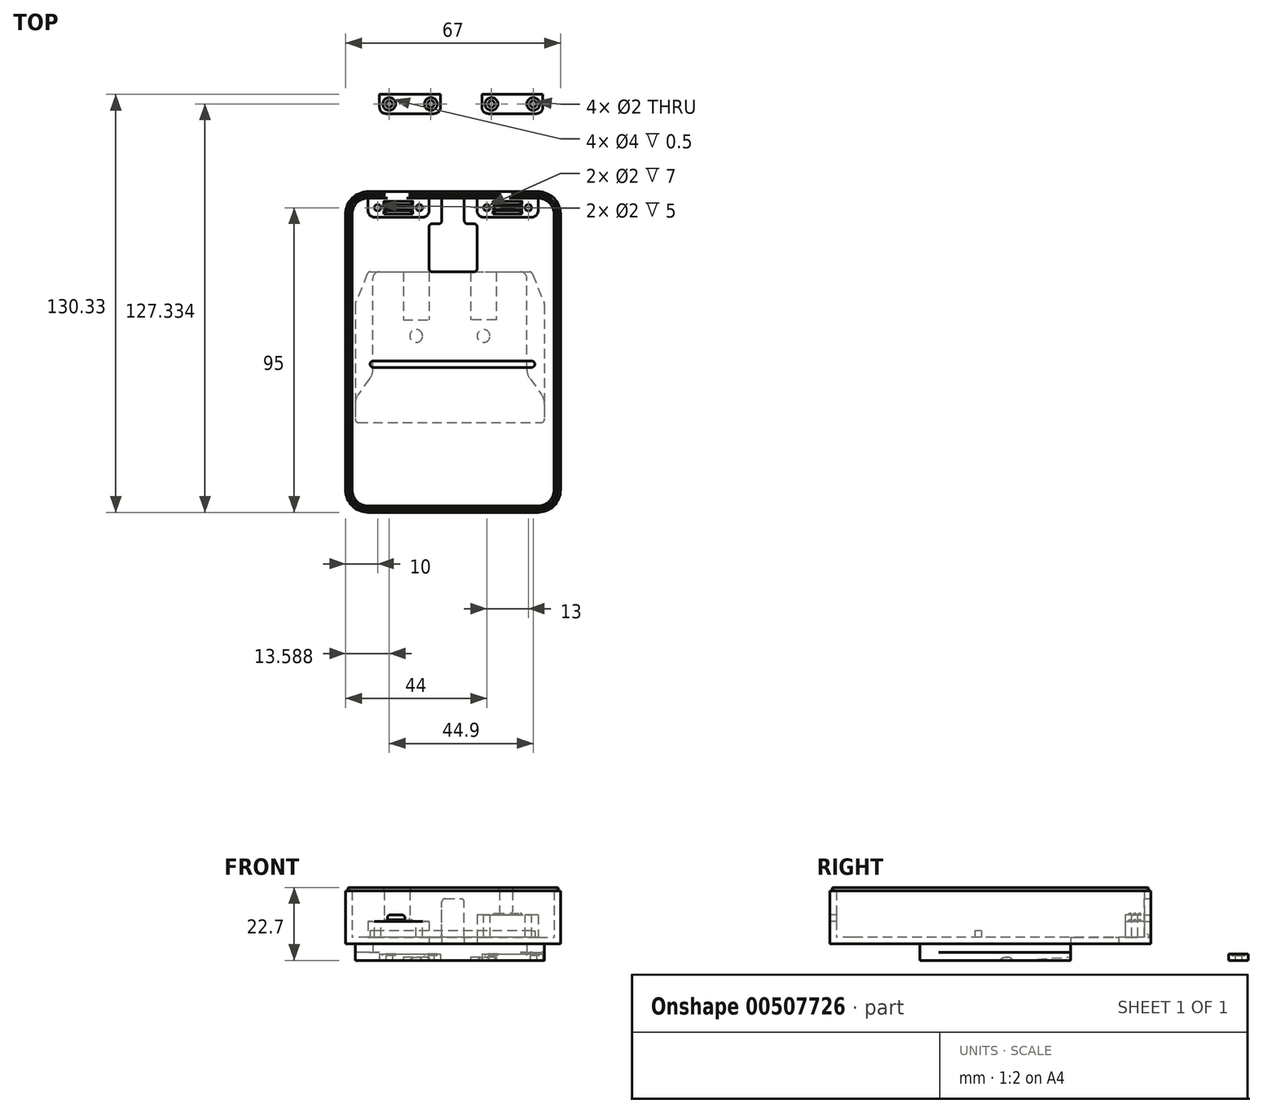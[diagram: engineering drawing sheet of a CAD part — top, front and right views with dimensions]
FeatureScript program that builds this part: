
annotation { "Feature Type Name" : "Feature", "Feature Type Description" : "" }
export const myFeature = defineFeature(function(context is Context, id is Id, definition is map)
    precondition{}
    {
        {
            var Q0;
            Q0=qCreatedBy(makeId("Top.planeOp"),FACE);
            var sketch = newSketch(context, id + "F0", { "sketchPlane" : qUnion([Q0])});
            skLineSegment(sketch, "E0.bottom", {"start": v(4, 0) * mm, "end": v(55, 0) * mm});
            skLineSegment(sketch, "E0.top", {"start": v(0, -47) * mm, "end": v(59, -47) * mm});
            skLineSegment(sketch, "E0.left", {"start": v(0, -10) * mm, "end": v(0, -47) * mm});
            skLineSegment(sketch, "E0.right", {"start": v(59, -10) * mm, "end": v(59, -47) * mm});
            skLineSegment(sketch, "E1", {"start": v(4, 0) * mm, "end": v(0, -10) * mm});
            skPoint(sketch, "E2.orphan", {"position": v(0, 0) * mm});
            skLineSegment(sketch, "E3", {"start": v(55, 0) * mm, "end": v(59, -10) * mm});
            skPoint(sketch, "E4.orphan", {"position": v(59, 0) * mm});
            skSolve(sketch);
        }
        {
            var Q0;
            Q0=makeQuery(id+"F0.imprint","IMPRINT",FACE,{"disambiguationData":[TD([[makeQuery(id+"F0.imprint","IMPRINT",EDGE,{"derivedFrom":sQuery(id+"F0.wireOp",EDGE,"E0.bottom")}),-1.0]])]});
            extrude(context, id + "F1", {"entities" : qUnion([Q0]), "depth" : 2.5 * mm, "offsetDistance" : 25 * mm});
        }
        {
            var Q0;
            Q0=makeQuery(id+"F1.opExtrude","CAP_FACE",FACE,{"disambiguationData":[OSD([sQuery(id+"F0.wireOp",EDGE,"E0.bottom"),sQuery(id+"F0.wireOp",EDGE,"E0.top"),sQuery(id+"F0.wireOp",EDGE,"E0.left"),sQuery(id+"F0.wireOp",EDGE,"E0.right"),sQuery(id+"F0.wireOp",EDGE,"E1"),sQuery(id+"F0.wireOp",EDGE,"E3")])],"isStart":false});
            var sketch = newSketch(context, id + "F2", { "sketchPlane" : qUnion([Q0])});
            skLineSegment(sketch, "E5.bottom", {"start": v(0, -47) * mm, "end": v(59, -47) * mm});
            skLineSegment(sketch, "E5.left", {"start": v(0, -47) * mm, "end": v(0, -39.5) * mm});
            skLineSegment(sketch, "E5.right", {"start": v(59, -47) * mm, "end": v(59, -39.5) * mm});
            skLineSegment(sketch, "E6.top", {"start": v(7.5, 0) * mm, "end": v(51.5, 0) * mm});
            skLineSegment(sketch, "E6.left", {"start": v(5.5, -32) * mm, "end": v(5.5, -2) * mm});
            skLineSegment(sketch, "E6.right", {"start": v(53.5, -32) * mm, "end": v(53.5, -2) * mm});
            skPoint(sketch, "E7.visualSharp", {"position": v(5.5, 0) * mm});
            skArc(sketch, "E7.filletArc", {"start": v(7.5, 0) * mm, "mid": v(6.09, -0.59) * mm, "end": v(5.5, -2) * mm});
            skPoint(sketch, "E8.visualSharp", {"position": v(53.5, 0) * mm});
            skArc(sketch, "E8.filletArc", {"start": v(53.5, -2) * mm, "mid": v(52.91, -0.59) * mm, "end": v(51.5, 0) * mm});
            skLineSegment(sketch, "E9", {"start": v(53.5, -32) * mm, "end": v(59, -39.5) * mm});
            skLineSegment(sketch, "E10", {"start": v(5.5, -32) * mm, "end": v(0, -39.5) * mm});
            skPoint(sketch, "E11.orphan", {"position": v(0, -32) * mm});
            skPoint(sketch, "E12.orphan", {"position": v(59, -32) * mm});
            skSolve(sketch);
        }
        {
            var Q0;
            Q0=makeQuery(id+"F2.imprint","IMPRINT",FACE,{"disambiguationData":[TD([[makeQuery(id+"F2.imprint","IMPRINT",EDGE,{"derivedFrom":sQuery(id+"F2.wireOp",EDGE,"E5.bottom")}),1.0]])]});
            extrude(context, id + "F3", {"entities" : qUnion([Q0]), "operationType" : NewBodyOperationType.ADD, "depth" : 2.7 * mm, "offsetDistance" : 25 * mm});
        }
        {
            var Q0;
            Q0=makeQuery(id+"F3.opExtrude","CAP_FACE",FACE,{"disambiguationData":[OSD([sQuery(id+"F2.wireOp",EDGE,"E5.bottom"),sQuery(id+"F2.wireOp",EDGE,"E5.left"),sQuery(id+"F2.wireOp",EDGE,"E5.right"),sQuery(id+"F2.wireOp",EDGE,"E6.top"),sQuery(id+"F2.wireOp",EDGE,"E6.left"),sQuery(id+"F2.wireOp",EDGE,"E6.right"),sQuery(id+"F2.wireOp",EDGE,"E7.filletArc"),sQuery(id+"F2.wireOp",EDGE,"E8.filletArc"),sQuery(id+"F2.wireOp",EDGE,"E9"),sQuery(id+"F2.wireOp",EDGE,"E10")])],"isStart":false});
            var sketch = newSketch(context, id + "F4", { "sketchPlane" : qUnion([Q0])});
            skLineSegment(sketch, "E13.bottom", {"start": v(57, -75) * mm, "end": v(4, -75) * mm});
            skLineSegment(sketch, "E13.top", {"start": v(57, 25) * mm, "end": v(35, 25) * mm});
            skLineSegment(sketch, "E13.left", {"start": v(64, -68) * mm, "end": v(64, 18) * mm});
            skLineSegment(sketch, "E13.right", {"start": v(-3, -68) * mm, "end": v(-3, 18) * mm});
            skPoint(sketch, "E14.visualSharp", {"position": v(-3, 25) * mm});
            skArc(sketch, "E14.filletArc", {"start": v(4, 25) * mm, "mid": v(-0.95, 22.95) * mm, "end": v(-3, 18) * mm});
            skPoint(sketch, "E15.visualSharp", {"position": v(64, 25) * mm});
            skArc(sketch, "E15.filletArc", {"start": v(64, 18) * mm, "mid": v(61.95, 22.95) * mm, "end": v(57, 25) * mm});
            skPoint(sketch, "E16.visualSharp", {"position": v(64, -75) * mm});
            skArc(sketch, "E16.filletArc", {"start": v(57, -75) * mm, "mid": v(61.95, -72.95) * mm, "end": v(64, -68) * mm});
            skPoint(sketch, "E17.visualSharp", {"position": v(-3, -75) * mm});
            skArc(sketch, "E17.filletArc", {"start": v(-3, -68) * mm, "mid": v(-0.95, -72.95) * mm, "end": v(4, -75) * mm});
            skLineSegment(sketch, "E18.top", {"start": v(27, 0) * mm, "end": v(34, 0) * mm});
            skLineSegment(sketch, "E18.left", {"start": v(27, 24) * mm, "end": v(27, 16) * mm});
            skLineSegment(sketch, "E18.right", {"start": v(34, 24) * mm, "end": v(34, 16) * mm});
            skLineSegment(sketch, "E19.filletArc", {"start": v(27, 0) * mm, "end": v(27, 0) * mm});
            skLineSegment(sketch, "E20.filletArc", {"start": v(34, 0) * mm, "end": v(34, 0) * mm});
            skLineSegment(sketch, "E21.trimOffspring", {"start": v(26, 25) * mm, "end": v(4, 25) * mm});
            skPoint(sketch, "E22.visualSharp", {"position": v(27, 25) * mm});
            skArc(sketch, "E22.filletArc", {"start": v(27, 24) * mm, "mid": v(26.7, 24.7) * mm, "end": v(26, 25) * mm});
            skPoint(sketch, "E23.visualSharp", {"position": v(34, 25) * mm});
            skArc(sketch, "E23.filletArc", {"start": v(35, 25) * mm, "mid": v(34.3, 24.7) * mm, "end": v(34, 24) * mm});
            skPoint(sketch, "E24", {"position": v(34, 15) * mm});
            skLineSegment(sketch, "E25", {"start": v(34, 0) * mm, "end": v(37, 0) * mm});
            skLineSegment(sketch, "E26", {"start": v(38, 1) * mm, "end": v(38, 14) * mm});
            skLineSegment(sketch, "E27", {"start": v(37, 15) * mm, "end": v(35, 15) * mm});
            skPoint(sketch, "E28", {"position": v(27, 15) * mm});
            skLineSegment(sketch, "E29", {"start": v(26, 15) * mm, "end": v(24, 15) * mm});
            skLineSegment(sketch, "E30", {"start": v(23, 14) * mm, "end": v(23, 1) * mm});
            skLineSegment(sketch, "E31", {"start": v(24, 0) * mm, "end": v(27, 0) * mm});
            skPoint(sketch, "E32.visualSharp", {"position": v(23, 15) * mm});
            skArc(sketch, "E32.filletArc", {"start": v(24, 15) * mm, "mid": v(23.3, 14.7) * mm, "end": v(23, 14) * mm});
            skPoint(sketch, "E33.visualSharp", {"position": v(23, 0) * mm});
            skArc(sketch, "E33.filletArc", {"start": v(23, 1) * mm, "mid": v(23.3, 0.3) * mm, "end": v(24, 0) * mm});
            skPoint(sketch, "E34.visualSharp", {"position": v(38, 0) * mm});
            skArc(sketch, "E34.filletArc", {"start": v(37, 0) * mm, "mid": v(37.7, 0.3) * mm, "end": v(38, 1) * mm});
            skPoint(sketch, "E35.visualSharp", {"position": v(38, 15) * mm});
            skArc(sketch, "E35.filletArc", {"start": v(38, 14) * mm, "mid": v(37.7, 14.7) * mm, "end": v(37, 15) * mm});
            skArc(sketch, "E36.filletArc", {"start": v(26, 15) * mm, "mid": v(26.7, 15.3) * mm, "end": v(27, 16) * mm});
            skArc(sketch, "E37.filletArc", {"start": v(34, 16) * mm, "mid": v(34.3, 15.3) * mm, "end": v(35, 15) * mm});
            skSolve(sketch);
        }
        {
            var Q0;
            Q0=qSketchRegion(id+"F4",true);
            extrude(context, id + "F5", {"entities" : qUnion([Q0]), "operationType" : NewBodyOperationType.ADD, "depth" : 2 * mm, "offsetDistance" : 25 * mm});
        }
        {
            var Q0;
            Q0=makeQuery(id+"F5.opExtrude","CAP_FACE",FACE,{"disambiguationData":[OSD([sQuery(id+"F4.wireOp",EDGE,"E13.bottom"),sQuery(id+"F4.wireOp",EDGE,"E13.top"),sQuery(id+"F4.wireOp",EDGE,"E13.left"),sQuery(id+"F4.wireOp",EDGE,"E13.right"),sQuery(id+"F4.wireOp",EDGE,"E14.filletArc"),sQuery(id+"F4.wireOp",EDGE,"E15.filletArc"),sQuery(id+"F4.wireOp",EDGE,"E16.filletArc"),sQuery(id+"F4.wireOp",EDGE,"E17.filletArc"),sQuery(id+"F4.wireOp",EDGE,"E18.top"),sQuery(id+"F4.wireOp",EDGE,"E18.left"),sQuery(id+"F4.wireOp",EDGE,"E18.right"),sQuery(id+"F4.wireOp",EDGE,"E19.filletArc"),sQuery(id+"F4.wireOp",EDGE,"E20.filletArc"),sQuery(id+"F4.wireOp",EDGE,"E21.trimOffspring"),sQuery(id+"F4.wireOp",EDGE,"E22.filletArc"),sQuery(id+"F4.wireOp",EDGE,"E23.filletArc")])],"isStart":false});
            var sketch = newSketch(context, id + "F6", { "sketchPlane" : qUnion([Q0])});
            skLineSegment(sketch, "E38.bottom", {"start": v(57, 25) * mm, "end": v(4, 25) * mm});
            skLineSegment(sketch, "E38.top", {"start": v(57, -75) * mm, "end": v(4, -75) * mm});
            skLineSegment(sketch, "E38.left", {"start": v(64, 18) * mm, "end": v(64, -68) * mm});
            skLineSegment(sketch, "E38.right", {"start": v(-3, 18) * mm, "end": v(-3, -68) * mm});
            skPoint(sketch, "E39.visualSharp", {"position": v(-3, 25) * mm});
            skArc(sketch, "E39.filletArc", {"start": v(4, 25) * mm, "mid": v(-0.95, 22.95) * mm, "end": v(-3, 18) * mm});
            skPoint(sketch, "E40.visualSharp", {"position": v(64, 25) * mm});
            skArc(sketch, "E40.filletArc", {"start": v(64, 18) * mm, "mid": v(61.95, 22.95) * mm, "end": v(57, 25) * mm});
            skPoint(sketch, "E41.visualSharp", {"position": v(64, -75) * mm});
            skArc(sketch, "E41.filletArc", {"start": v(57, -75) * mm, "mid": v(61.95, -72.95) * mm, "end": v(64, -68) * mm});
            skPoint(sketch, "E42.visualSharp", {"position": v(-3, -75) * mm});
            skArc(sketch, "E42.filletArc", {"start": v(-3, -68) * mm, "mid": v(-0.95, -72.95) * mm, "end": v(4, -75) * mm});
            skArc(sketch, "E43.0", {"start": v(62, 18) * mm, "mid": v(60.54, 21.54) * mm, "end": v(57, 23) * mm});
            skLineSegment(sketch, "E43.1", {"start": v(62, 18) * mm, "end": v(62, -68) * mm});
            skLineSegment(sketch, "E43.2", {"start": v(57, 23) * mm, "end": v(4, 23) * mm});
            skArc(sketch, "E43.3", {"start": v(57, -73) * mm, "mid": v(60.54, -71.54) * mm, "end": v(62, -68) * mm});
            skArc(sketch, "E43.4", {"start": v(4, 23) * mm, "mid": v(0.46, 21.54) * mm, "end": v(-1, 18) * mm});
            skLineSegment(sketch, "E43.5", {"start": v(-1, 18) * mm, "end": v(-1, -68) * mm});
            skArc(sketch, "E43.6", {"start": v(-1, -68) * mm, "mid": v(0.46, -71.54) * mm, "end": v(4, -73) * mm});
            skLineSegment(sketch, "E43.7", {"start": v(57, -73) * mm, "end": v(4, -73) * mm});
            skSolve(sketch);
        }
        {
            var Q0;
            Q0=qSketchRegion(id+"F6",true);
            extrude(context, id + "F7", {"entities" : qUnion([Q0]), "operationType" : NewBodyOperationType.ADD, "depth" : 14.5 * mm, "offsetDistance" : 25 * mm});
        }
        {
            var Q0;
            Q0=makeQuery(id+"F7.boolean.opBoolean","MERGE",FACE,{"derivedFrom":[makeQuery(id+"F5.opExtrude","SWEPT_FACE",FACE,{"disambiguationData":[OSD([sQuery(id+"F4.wireOp",EDGE,"E13.top")])]}),makeQuery(id+"F5.opExtrude","SWEPT_FACE",FACE,{"disambiguationData":[OSD([sQuery(id+"F4.wireOp",EDGE,"E21.trimOffspring")])]}),makeQuery(id+"F7.opExtrude","SWEPT_FACE",FACE,{"disambiguationData":[OSD([sQuery(id+"F6.wireOp",EDGE,"E38.bottom")])]})]});
            var sketch = newSketch(context, id + "F8", { "sketchPlane" : qUnion([Q0])});
            skLineSegment(sketch, "E44.bottom", {"start": v(-27, 7.2) * mm, "end": v(-34, 7.2) * mm});
            skLineSegment(sketch, "E44.top", {"start": v(-28, 19.2) * mm, "end": v(-33, 19.2) * mm});
            skLineSegment(sketch, "E44.left", {"start": v(-27, 7.2) * mm, "end": v(-27, 18.2) * mm});
            skLineSegment(sketch, "E44.right", {"start": v(-34, 7.2) * mm, "end": v(-34, 18.2) * mm});
            skPoint(sketch, "E45.visualSharp", {"position": v(-34, 19.2) * mm});
            skArc(sketch, "E45.filletArc", {"start": v(-33, 19.2) * mm, "mid": v(-33.7, 18.9) * mm, "end": v(-34, 18.2) * mm});
            skPoint(sketch, "E46.visualSharp", {"position": v(-27, 19.2) * mm});
            skArc(sketch, "E46.filletArc", {"start": v(-27, 18.2) * mm, "mid": v(-27.3, 18.9) * mm, "end": v(-28, 19.2) * mm});
            skLineSegment(sketch, "E47.bottom", {"start": v(-49, 21.7) * mm, "end": v(-45, 21.7) * mm});
            skLineSegment(sketch, "E47.top", {"start": v(-48, 14.2) * mm, "end": v(-46, 14.2) * mm});
            skLineSegment(sketch, "E47.left", {"start": v(-49, 21.7) * mm, "end": v(-49, 15.2) * mm});
            skLineSegment(sketch, "E47.right", {"start": v(-45, 21.7) * mm, "end": v(-45, 15.2) * mm});
            skPoint(sketch, "E48.visualSharp", {"position": v(-49, 14.2) * mm});
            skArc(sketch, "E48.filletArc", {"start": v(-49, 15.2) * mm, "mid": v(-48.7, 14.5) * mm, "end": v(-48, 14.2) * mm});
            skPoint(sketch, "E49.visualSharp", {"position": v(-45, 14.2) * mm});
            skArc(sketch, "E49.filletArc", {"start": v(-46, 14.2) * mm, "mid": v(-45.3, 14.5) * mm, "end": v(-45, 15.2) * mm});
            skLineSegment(sketch, "E50.bottom", {"start": v(-9, 21.7) * mm, "end": v(-17, 21.7) * mm});
            skLineSegment(sketch, "E50.top", {"start": v(-10, 12.2) * mm, "end": v(-16, 12.2) * mm});
            skLineSegment(sketch, "E50.left", {"start": v(-9, 21.7) * mm, "end": v(-9, 13.2) * mm});
            skLineSegment(sketch, "E50.right", {"start": v(-17, 21.7) * mm, "end": v(-17, 13.2) * mm});
            skPoint(sketch, "E51.visualSharp", {"position": v(-17, 12.2) * mm});
            skArc(sketch, "E51.filletArc", {"start": v(-17, 13.2) * mm, "mid": v(-16.7, 12.5) * mm, "end": v(-16, 12.2) * mm});
            skPoint(sketch, "E52.visualSharp", {"position": v(-9, 12.2) * mm});
            skArc(sketch, "E52.filletArc", {"start": v(-10, 12.2) * mm, "mid": v(-9.3, 12.5) * mm, "end": v(-9, 13.2) * mm});
            skSolve(sketch);
        }
        {
            var Q0;
            Q0=makeQuery(id+"FvWDrRj3cYPkLqx_1.boolean.opBoolean","MERGE",FACE,{"derivedFrom":[makeQuery(id+"F5.opExtrude","CAP_FACE",FACE,{"disambiguationData":[OSD([sQuery(id+"F4.wireOp",EDGE,"E13.bottom"),sQuery(id+"F4.wireOp",EDGE,"E13.top"),sQuery(id+"F4.wireOp",EDGE,"E13.left"),sQuery(id+"F4.wireOp",EDGE,"E13.right"),sQuery(id+"F4.wireOp",EDGE,"E14.filletArc"),sQuery(id+"F4.wireOp",EDGE,"E15.filletArc"),sQuery(id+"F4.wireOp",EDGE,"E16.filletArc"),sQuery(id+"F4.wireOp",EDGE,"E17.filletArc"),sQuery(id+"F4.wireOp",EDGE,"E18.top"),sQuery(id+"F4.wireOp",EDGE,"E18.left"),sQuery(id+"F4.wireOp",EDGE,"E18.right"),sQuery(id+"F4.wireOp",EDGE,"E19.filletArc"),sQuery(id+"F4.wireOp",EDGE,"E20.filletArc"),sQuery(id+"F4.wireOp",EDGE,"E21.trimOffspring"),sQuery(id+"F4.wireOp",EDGE,"E22.filletArc"),sQuery(id+"F4.wireOp",EDGE,"E23.filletArc")])],"isStart":false}),makeQuery(id+"FvWDrRj3cYPkLqx_1.opExtrude","SWEPT_FACE",FACE,{"disambiguationData":[OSD([sQuery(id+"F8.wireOp",EDGE,"E44.bottom")])]})]});
            var sketch = newSketch(context, id + "F9", { "sketchPlane" : qUnion([Q0])});
            skLineSegment(sketch, "E53.bottom", {"start": v(54.99, -29.8) * mm, "end": v(5.63, -29.8) * mm});
            skLineSegment(sketch, "E53.top", {"start": v(54.99, -27.8) * mm, "end": v(5.63, -27.8) * mm});
            skLineSegment(sketch, "E53.left", {"start": v(55.99, -28.8) * mm, "end": v(55.99, -28.8) * mm});
            skLineSegment(sketch, "E53.right", {"start": v(4.63, -28.8) * mm, "end": v(4.63, -28.8) * mm});
            skPoint(sketch, "E54.visualSharp", {"position": v(4.63, -27.8) * mm});
            skArc(sketch, "E54.filletArc", {"start": v(5.63, -27.8) * mm, "mid": v(4.92, -28.1) * mm, "end": v(4.63, -28.8) * mm});
            skPoint(sketch, "E55.visualSharp", {"position": v(4.63, -29.8) * mm});
            skArc(sketch, "E55.filletArc", {"start": v(4.63, -28.8) * mm, "mid": v(4.92, -29.5) * mm, "end": v(5.63, -29.8) * mm});
            skPoint(sketch, "E56.visualSharp", {"position": v(55.99, -27.8) * mm});
            skArc(sketch, "E56.filletArc", {"start": v(55.99, -28.8) * mm, "mid": v(55.7, -28.1) * mm, "end": v(54.99, -27.8) * mm});
            skPoint(sketch, "E57.visualSharp", {"position": v(55.99, -29.8) * mm});
            skArc(sketch, "E57.filletArc", {"start": v(54.99, -29.8) * mm, "mid": v(55.7, -29.5) * mm, "end": v(55.99, -28.8) * mm});
            skSolve(sketch);
        }
        {
            var Q0;
            Q0=qSketchRegion(id+"F9",true);
            var Q1;
            Q1=qSketchRegion(id+"F11",true);
            extrude(context, id + "F10", {"entities" : qUnion([Q0, Q1]), "operationType" : NewBodyOperationType.ADD, "depth" : 2 * mm});
        }
        {
            var Q0;
            Q0=makeQuery(id+"FvWDrRj3cYPkLqx_1.boolean.opBoolean","MERGE",FACE,{"derivedFrom":[makeQuery(id+"F5.opExtrude","CAP_FACE",FACE,{"disambiguationData":[OSD([sQuery(id+"F4.wireOp",EDGE,"E13.bottom"),sQuery(id+"F4.wireOp",EDGE,"E13.top"),sQuery(id+"F4.wireOp",EDGE,"E13.left"),sQuery(id+"F4.wireOp",EDGE,"E13.right"),sQuery(id+"F4.wireOp",EDGE,"E14.filletArc"),sQuery(id+"F4.wireOp",EDGE,"E15.filletArc"),sQuery(id+"F4.wireOp",EDGE,"E16.filletArc"),sQuery(id+"F4.wireOp",EDGE,"E17.filletArc"),sQuery(id+"F4.wireOp",EDGE,"E18.top"),sQuery(id+"F4.wireOp",EDGE,"E18.left"),sQuery(id+"F4.wireOp",EDGE,"E18.right"),sQuery(id+"F4.wireOp",EDGE,"E19.filletArc"),sQuery(id+"F4.wireOp",EDGE,"E20.filletArc"),sQuery(id+"F4.wireOp",EDGE,"E21.trimOffspring"),sQuery(id+"F4.wireOp",EDGE,"E22.filletArc"),sQuery(id+"F4.wireOp",EDGE,"E23.filletArc")])],"isStart":false}),makeQuery(id+"FvWDrRj3cYPkLqx_1.opExtrude","SWEPT_FACE",FACE,{"disambiguationData":[OSD([sQuery(id+"F8.wireOp",EDGE,"E44.bottom")])]})]});
            var sketch = newSketch(context, id + "F11", { "sketchPlane" : qUnion([Q0])});
            skSolve(sketch);
        }
        {
            var Q0;
            Q0=makeQuery(id+"F8.imprint","IMPRINT",FACE,{"disambiguationData":[TD([[makeQuery(id+"F8.imprint","IMPRINT",EDGE,{"derivedFrom":sQuery(id+"F8.wireOp",EDGE,"E47.bottom")}),-1.0]])]});
            var Q1;
            Q1=makeQuery(id+"F8.imprint","IMPRINT",FACE,{"disambiguationData":[TD([[makeQuery(id+"F8.imprint","IMPRINT",EDGE,{"derivedFrom":sQuery(id+"F8.wireOp",EDGE,"E44.top")}),1.0]])]});
            var Q2;
            Q2=makeQuery(id+"F8.imprint","IMPRINT",FACE,{"disambiguationData":[TD([[makeQuery(id+"F8.imprint","IMPRINT",EDGE,{"derivedFrom":sQuery(id+"F8.wireOp",EDGE,"E50.bottom")}),-1.0]])]});
            extrude(context, id + "F12", {"entities" : qUnion([Q0, Q1, Q2]), "operationType" : NewBodyOperationType.REMOVE, "oppositeDirection" : true, "depth" : 2 * mm});
        }
        {
            var Q0;
            Q0=makeQuery(id+"F7.boolean.opBoolean","MERGE",FACE,{"derivedFrom":[makeQuery(id+"F5.opExtrude","SWEPT_FACE",FACE,{"disambiguationData":[OSD([sQuery(id+"F4.wireOp",EDGE,"E13.bottom")])]}),makeQuery(id+"F7.opExtrude","SWEPT_FACE",FACE,{"disambiguationData":[OSD([sQuery(id+"F6.wireOp",EDGE,"E38.top")])]})]});
            var sketch = newSketch(context, id + "F13", { "sketchPlane" : qUnion([Q0])});
            skLineSegment(sketch, "E58.bottom", {"start": v(11, 14.2) * mm, "end": v(14.5, 14.2) * mm});
            skLineSegment(sketch, "E58.top", {"start": v(11, 12.2) * mm, "end": v(14.5, 12.2) * mm});
            skLineSegment(sketch, "E58.left", {"start": v(10, 13.2) * mm, "end": v(10, 13.2) * mm});
            skLineSegment(sketch, "E58.right", {"start": v(15.5, 13.2) * mm, "end": v(15.5, 13.2) * mm});
            skPoint(sketch, "E59.visualSharp", {"position": v(10, 14.2) * mm});
            skArc(sketch, "E59.filletArc", {"start": v(11, 14.2) * mm, "mid": v(10.3, 13.9) * mm, "end": v(10, 13.2) * mm});
            skPoint(sketch, "E60.visualSharp", {"position": v(10, 12.2) * mm});
            skArc(sketch, "E60.filletArc", {"start": v(10, 13.2) * mm, "mid": v(10.3, 12.5) * mm, "end": v(11, 12.2) * mm});
            skPoint(sketch, "E61.visualSharp", {"position": v(15.5, 14.2) * mm});
            skArc(sketch, "E61.filletArc", {"start": v(15.5, 13.2) * mm, "mid": v(15.2, 13.9) * mm, "end": v(14.5, 14.2) * mm});
            skPoint(sketch, "E62.visualSharp", {"position": v(15.5, 12.2) * mm});
            skArc(sketch, "E62.filletArc", {"start": v(14.5, 12.2) * mm, "mid": v(15.2, 12.5) * mm, "end": v(15.5, 13.2) * mm});
            skSolve(sketch);
        }
        {
            var Q0;
            Q0=makeQuery(id+"F13.imprint","IMPRINT",FACE,{"disambiguationData":[TD([[makeQuery(id+"F13.imprint","IMPRINT",EDGE,{"derivedFrom":sQuery(id+"F13.wireOp",EDGE,"E58.bottom")}),-1.0]])]});
            extrude(context, id + "F14", {"entities" : qUnion([Q0]), "operationType" : NewBodyOperationType.REMOVE, "oppositeDirection" : true, "depth" : 2 * mm, "offsetDistance" : 25 * mm});
        }
        {
            var Q0;
            Q0=makeQuery(id+"F3.boolean.opBoolean","MERGE",EDGE,{"derivedFrom":[makeQuery(id+"F1.opExtrude","SWEPT_EDGE",EDGE,{"disambiguationData":[OSD([sQuery(id+"F0.wireOp",EDGE,"E0.top"),sQuery(id+"F0.wireOp",EDGE,"E0.left")])]}),makeQuery(id+"F3.opExtrude","SWEPT_EDGE",EDGE,{"disambiguationData":[OSD([sQuery(id+"F2.wireOp",EDGE,"E5.bottom"),sQuery(id+"F2.wireOp",EDGE,"E5.left")])]})]});
            var Q1;
            Q1=makeQuery(id+"F3.boolean.opBoolean","MERGE",EDGE,{"derivedFrom":[makeQuery(id+"F1.opExtrude","SWEPT_EDGE",EDGE,{"disambiguationData":[OSD([sQuery(id+"F0.wireOp",EDGE,"E0.top"),sQuery(id+"F0.wireOp",EDGE,"E0.right")])]}),makeQuery(id+"F3.opExtrude","SWEPT_EDGE",EDGE,{"disambiguationData":[OSD([sQuery(id+"F2.wireOp",EDGE,"E5.bottom"),sQuery(id+"F2.wireOp",EDGE,"E5.right")])]})]});
            var Q2;
            Q2=makeQuery(id+"F1.opExtrude","SWEPT_EDGE",EDGE,{"disambiguationData":[OSD([sQuery(id+"F0.wireOp",EDGE,"E0.bottom"),sQuery(id+"F0.wireOp",EDGE,"E1")])]});
            var Q3;
            Q3=makeQuery(id+"F1.opExtrude","SWEPT_EDGE",EDGE,{"disambiguationData":[OSD([sQuery(id+"F0.wireOp",EDGE,"E0.bottom"),sQuery(id+"F0.wireOp",EDGE,"E3")])]});
            var Q4;
            Q4=makeQuery(id+"F1.opExtrude","SWEPT_EDGE",EDGE,{"disambiguationData":[OSD([sQuery(id+"F0.wireOp",EDGE,"E0.right"),sQuery(id+"F0.wireOp",EDGE,"E3")])]});
            var Q5;
            Q5=makeQuery(id+"F1.opExtrude","SWEPT_EDGE",EDGE,{"disambiguationData":[OSD([sQuery(id+"F0.wireOp",EDGE,"E0.left"),sQuery(id+"F0.wireOp",EDGE,"E1")])]});
            fillet(context, id + "F15", {"entities" : qUnion([Q0, Q1, Q2, Q3, Q4, Q5]), "radius" : 1 * mm, "tangentPropagation" : true, "allowEdgeOverflow" : false});
        }
        {
            var Q0;
            Q0=makeQuery(id+"F3.opExtrude","SWEPT_EDGE",EDGE,{"disambiguationData":[OSD([sQuery(id+"F0.wireOp",EDGE,"E0.left"),sQuery(id+"F2.wireOp",EDGE,"E5.left"),sQuery(id+"F2.wireOp",EDGE,"E10")])]});
            var Q1;
            Q1=makeQuery(id+"F3.opExtrude","SWEPT_EDGE",EDGE,{"disambiguationData":[OSD([sQuery(id+"F0.wireOp",EDGE,"E0.right"),sQuery(id+"F2.wireOp",EDGE,"E5.right"),sQuery(id+"F2.wireOp",EDGE,"E9")])]});
            var Q2;
            Q2=makeQuery(id+"F3.opExtrude","SWEPT_EDGE",EDGE,{"disambiguationData":[OSD([sQuery(id+"F2.wireOp",EDGE,"E6.right"),sQuery(id+"F2.wireOp",EDGE,"E9")])]});
            var Q3;
            Q3=makeQuery(id+"F3.opExtrude","SWEPT_EDGE",EDGE,{"disambiguationData":[OSD([sQuery(id+"F2.wireOp",EDGE,"E6.left"),sQuery(id+"F2.wireOp",EDGE,"E10")])]});
            fillet(context, id + "F16", {"entities" : qUnion([Q0, Q1, Q2, Q3]), "radius" : 5 * mm, "tangentPropagation" : true, "allowEdgeOverflow" : false});
        }
        {
            var Q0;
            Q0=makeQuery(id+"F1.opExtrude","CAP_FACE",FACE,{"disambiguationData":[OSD([sQuery(id+"F0.wireOp",EDGE,"E0.bottom"),sQuery(id+"F0.wireOp",EDGE,"E0.top"),sQuery(id+"F0.wireOp",EDGE,"E0.left"),sQuery(id+"F0.wireOp",EDGE,"E0.right"),sQuery(id+"F0.wireOp",EDGE,"E1"),sQuery(id+"F0.wireOp",EDGE,"E3")])],"isStart":true});
            var sketch = newSketch(context, id + "F17", { "sketchPlane" : qUnion([Q0])});
            skLineSegment(sketch, "E63.bottom", {"start": v(15, 0) * mm, "end": v(23, 0) * mm});
            skLineSegment(sketch, "E63.top", {"start": v(15, 15) * mm, "end": v(23, 15) * mm});
            skLineSegment(sketch, "E63.left", {"start": v(15, 0) * mm, "end": v(15, 15) * mm});
            skLineSegment(sketch, "E63.right", {"start": v(23, 0) * mm, "end": v(23, 15) * mm});
            skLineSegment(sketch, "E64.bottom", {"start": v(44, 0) * mm, "end": v(36, 0) * mm});
            skLineSegment(sketch, "E64.top", {"start": v(44, 15) * mm, "end": v(36, 15) * mm});
            skLineSegment(sketch, "E64.left", {"start": v(44, 0) * mm, "end": v(44, 15) * mm});
            skLineSegment(sketch, "E64.right", {"start": v(36, 0) * mm, "end": v(36, 15) * mm});
            skSolve(sketch);
        }
        {
            var Q0;
            Q0=makeQuery(id+"F1.opExtrude","CAP_FACE",FACE,{"disambiguationData":[OSD([sQuery(id+"F0.wireOp",EDGE,"E0.bottom"),sQuery(id+"F0.wireOp",EDGE,"E0.top"),sQuery(id+"F0.wireOp",EDGE,"E0.left"),sQuery(id+"F0.wireOp",EDGE,"E0.right"),sQuery(id+"F0.wireOp",EDGE,"E1"),sQuery(id+"F0.wireOp",EDGE,"E3")])],"isStart":true});
            var sketch = newSketch(context, id + "F18", { "sketchPlane" : qUnion([Q0])});
            skCircle(sketch, "E65", {"center": v(19, 20) * mm, "radius": 2 * mm});
            skCircle(sketch, "E66", {"center": v(40, 20) * mm, "radius": 2 * mm});
            skSolve(sketch);
        }
        {
            var Q0;
            Q0=qSketchRegion(id+"F18",true);
            extrude(context, id + "F19", {"entities" : qUnion([Q0]), "operationType" : NewBodyOperationType.REMOVE, "oppositeDirection" : true, "depth" : 1 * mm});
        }
        {
            var Q0;
            Q0=makeQuery(id+"F17.imprint","IMPRINT",FACE,{"disambiguationData":[TD([[makeQuery(id+"F17.imprint","IMPRINT",EDGE,{"derivedFrom":sQuery(id+"F17.wireOp",EDGE,"E64.bottom")}),1.0]])]});
            var Q1;
            Q1=makeQuery(id+"F17.imprint","IMPRINT",FACE,{"disambiguationData":[TD([[makeQuery(id+"F17.imprint","IMPRINT",EDGE,{"derivedFrom":sQuery(id+"F17.wireOp",EDGE,"E63.bottom")}),1.0]])]});
            extrude(context, id + "F20", {"entities" : qUnion([Q0, Q1]), "operationType" : NewBodyOperationType.REMOVE, "oppositeDirection" : true, "depth" : 1.1 * mm});
        }
        {
            var Q0;
            Q0=makeQuery(id+"F20.boolean.opBoolean","COPY",EDGE,{"derivedFrom":makeQuery(id+"F20.opExtrude","CAP_EDGE",EDGE,{"disambiguationData":[OSD([sQuery(id+"F17.wireOp",EDGE,"E63.top")])],"isStart":false})});
            chamfer(context, id + "F21", {"entities" : qUnion([Q0]), "chamferType" : ChamferType.TWO_OFFSETS, "width1" : 1.1 * mm, "oppositeDirection" : false, "width2" : 15 * mm, "tangentPropagation" : true});
        }
        {
            var Q0;
            Q0=makeQuery(id+"F20.boolean.opBoolean","COPY",EDGE,{"derivedFrom":makeQuery(id+"F20.opExtrude","CAP_EDGE",EDGE,{"disambiguationData":[OSD([sQuery(id+"F17.wireOp",EDGE,"E64.top")])],"isStart":false})});
            chamfer(context, id + "F22", {"entities" : qUnion([Q0]), "chamferType" : ChamferType.TWO_OFFSETS, "width1" : 15 * mm, "oppositeDirection" : false, "width2" : 1.1 * mm, "tangentPropagation" : true});
        }
        {
            var Q0;
            Q0=makeQuery(id+"F19.boolean.opBoolean","COPY",EDGE,{"derivedFrom":makeQuery(id+"F19.opExtrude","CAP_EDGE",EDGE,{"disambiguationData":[OSD([sQuery(id+"F18.wireOp",EDGE,"E66")])],"isStart":false})});
            var Q1;
            Q1=makeQuery(id+"F19.boolean.opBoolean","COPY",EDGE,{"derivedFrom":makeQuery(id+"F19.opExtrude","CAP_EDGE",EDGE,{"disambiguationData":[OSD([sQuery(id+"F18.wireOp",EDGE,"E65")])],"isStart":false})});
            fillet(context, id + "F23", {"entities" : qUnion([Q0, Q1]), "radius" : 2 * mm, "tangentPropagation" : true, "allowEdgeOverflow" : false});
        }
        {
            var Q0;
            {var subQ0=sQuery(id+"F6.wireOp",EDGE,"E43.2");var subQ1=sQuery(id+"F6.wireOp",EDGE,"E43.1");var subQ2=sQuery(id+"F6.wireOp",EDGE,"E42.filletArc");var subQ3=sQuery(id+"F6.wireOp",EDGE,"E41.filletArc");var subQ4=sQuery(id+"F6.wireOp",EDGE,"E40.filletArc");var subQ5=sQuery(id+"F6.wireOp",EDGE,"E39.filletArc");var subQ6=sQuery(id+"F6.wireOp",EDGE,"E38.right");var subQ7=sQuery(id+"F6.wireOp",EDGE,"E38.left");var subQ8=sQuery(id+"F6.wireOp",EDGE,"E38.top");var subQ9=sQuery(id+"F6.wireOp",EDGE,"E43.4");var subQ10=sQuery(id+"F6.wireOp",EDGE,"E43.3");var subQ11=sQuery(id+"F6.wireOp",EDGE,"E38.bottom");var subQ12=sQuery(id+"F6.wireOp",EDGE,"E43.0");var subQ13=sQuery(id+"F6.wireOp",EDGE,"E43.5");var subQ14=sQuery(id+"F6.wireOp",EDGE,"E43.6");var subQ15=sQuery(id+"F6.wireOp",EDGE,"E43.7");Q0=makeQuery(id+"F12.boolean.opBoolean","SPLIT",FACE,{"disambiguationData":[TD([makeQuery(id+"F5.opExtrude","SWEPT_FACE",FACE,{"disambiguationData":[OSD([sQuery(id+"F4.wireOp",EDGE,"E13.bottom")])]})])],"derivedFrom":makeQuery(id+"F7.opExtrude","CAP_FACE",FACE,{"disambiguationData":[OSD([subQ11,subQ8,subQ7,subQ6,subQ5,subQ4,subQ3,subQ2,subQ12,subQ1,subQ0,subQ10,subQ9,subQ13,subQ14,subQ15])],"isStart":false})});}
            var sketch = newSketch(context, id + "F24", { "sketchPlane" : qUnion([Q0])});
            skLineSegment(sketch, "E67.0", {"start": v(57, 24.25) * mm, "end": v(49, 24.25) * mm});
            skArc(sketch, "E67.1", {"start": v(63.25, 18) * mm, "mid": v(61.42, 22.42) * mm, "end": v(57, 24.25) * mm});
            skLineSegment(sketch, "E67.2", {"start": v(63.25, -68) * mm, "end": v(63.25, 18) * mm});
            skArc(sketch, "E67.3", {"start": v(57, -74.25) * mm, "mid": v(61.42, -72.42) * mm, "end": v(63.25, -68) * mm});
            skLineSegment(sketch, "E67.4", {"start": v(57, -74.25) * mm, "end": v(4, -74.25) * mm});
            skLineSegment(sketch, "E67.5", {"start": v(9, 24.25) * mm, "end": v(4, 24.25) * mm});
            skArc(sketch, "E67.6", {"start": v(4, 24.25) * mm, "mid": v(-0.42, 22.42) * mm, "end": v(-2.25, 18) * mm});
            skLineSegment(sketch, "E67.7", {"start": v(-2.25, -68) * mm, "end": v(-2.25, 18) * mm});
            skArc(sketch, "E67.8", {"start": v(-2.25, -68) * mm, "mid": v(-0.42, -72.42) * mm, "end": v(4, -74.25) * mm});
            skLineSegment(sketch, "E68.0", {"start": v(57, 23.75) * mm, "end": v(49, 23.75) * mm});
            skArc(sketch, "E68.1", {"start": v(62.75, 18) * mm, "mid": v(61.07, 22.07) * mm, "end": v(57, 23.75) * mm});
            skLineSegment(sketch, "E68.2", {"start": v(62.75, 18) * mm, "end": v(62.75, -68) * mm});
            skArc(sketch, "E68.3", {"start": v(57, -73.75) * mm, "mid": v(61.07, -72.07) * mm, "end": v(62.75, -68) * mm});
            skLineSegment(sketch, "E68.4", {"start": v(57, -73.75) * mm, "end": v(4, -73.75) * mm});
            skLineSegment(sketch, "E68.5", {"start": v(9, 23.75) * mm, "end": v(4, 23.75) * mm});
            skArc(sketch, "E68.6", {"start": v(4, 23.75) * mm, "mid": v(-0.07, 22.07) * mm, "end": v(-1.75, 18) * mm});
            skLineSegment(sketch, "E68.7", {"start": v(-1.75, 18) * mm, "end": v(-1.75, -68) * mm});
            skArc(sketch, "E68.8", {"start": v(-1.75, -68) * mm, "mid": v(-0.07, -72.07) * mm, "end": v(4, -73.75) * mm});
            skLineSegment(sketch, "E69.0", {"start": v(45, 24.25) * mm, "end": v(17, 24.25) * mm});
            skLineSegment(sketch, "E70.0", {"start": v(45, 23.75) * mm, "end": v(17, 23.75) * mm});
            skLineSegment(sketch, "E71", {"start": v(17, 24.25) * mm, "end": v(17, 23.75) * mm});
            skLineSegment(sketch, "E72", {"start": v(45, 24.25) * mm, "end": v(45, 23.75) * mm});
            skSolve(sketch);
        }
        {
            var Q0;
            {var subQ2=sQuery(id+"F24.wireOp",EDGE,"E67.0");Q0=makeQuery(id+"F24.imprint","IMPRINT",FACE,{"disambiguationData":[TD([[makeQuery(id+"F24.imprint","IMPRINT",EDGE,{"derivedFrom":subQ2}),1.0]])]});}
            extrude(context, id + "F25", {"entities" : qUnion([Q0]), "operationType" : NewBodyOperationType.ADD, "depth" : 1 * mm, "offsetDistance" : 25 * mm});
        }
        {
            var Q0;
            Q0=qSketchRegion(id+"F24",true);
            extrude(context, id + "F26", {"entities" : qUnion([Q0]), "operationType" : NewBodyOperationType.ADD, "depth" : 1 * mm, "offsetDistance" : 25 * mm});
        }
        {
            var Q0;
            Q0=makeQuery(id+"F25.opExtrude","CAP_EDGE",EDGE,{"disambiguationData":[OSD([sQuery(id+"F6.wireOp",EDGE,"E38.bottom"),sQuery(id+"F8.wireOp",EDGE,"E47.bottom"),sQuery(id+"F8.wireOp",EDGE,"E47.left")])],"isStart":false});
            var Q1;
            Q1=makeQuery(id+"F26.opExtrude","CAP_EDGE",EDGE,{"disambiguationData":[OSD([sQuery(id+"F24.wireOp",EDGE,"E72")])],"isStart":false});
            var Q2;
            Q2=makeQuery(id+"F26.opExtrude","CAP_EDGE",EDGE,{"disambiguationData":[OSD([sQuery(id+"F24.wireOp",EDGE,"E71")])],"isStart":false});
            var Q3;
            Q3=makeQuery(id+"F25.opExtrude","CAP_EDGE",EDGE,{"disambiguationData":[OSD([sQuery(id+"F6.wireOp",EDGE,"E38.bottom"),sQuery(id+"F8.wireOp",EDGE,"E50.bottom"),sQuery(id+"F8.wireOp",EDGE,"E50.left")])],"isStart":false});
            var Q4;
            Q4=makeQuery(id+"F12.boolean.opBoolean","COPY",EDGE,{"derivedFrom":makeQuery(id+"F12.opExtrude","SWEPT_EDGE",EDGE,{"disambiguationData":[OSD([sQuery(id+"F8.wireOp",EDGE,"E44.bottom"),sQuery(id+"F8.wireOp",EDGE,"E44.right")])]})});
            var Q5;
            Q5=makeQuery(id+"F12.boolean.opBoolean","COPY",EDGE,{"derivedFrom":makeQuery(id+"F12.opExtrude","SWEPT_EDGE",EDGE,{"disambiguationData":[OSD([sQuery(id+"F8.wireOp",EDGE,"E44.bottom"),sQuery(id+"F8.wireOp",EDGE,"E44.left")])]})});
            fillet(context, id + "F27", {"entities" : qUnion([Q0, Q1, Q2, Q3, Q4, Q5]), "radius" : 1 * mm, "tangentPropagation" : true, "allowEdgeOverflow" : false});
        }
        {
            var Q0;
            {var subQ6=sQuery(id+"F4.wireOp",EDGE,"E18.top");Q0=makeQuery(id+"F11.imprint","IMPRINT",FACE,{"disambiguationData":[TD([[makeQuery(id+"F11.imprint","IMPRINT",EDGE,{"derivedFrom":makeQuery(id+"F5.opExtrude","CAP_EDGE",EDGE,{"disambiguationData":[OSD([subQ6])],"isStart":false})}),-1.0]])]});}
            var sketch = newSketch(context, id + "F28", { "sketchPlane" : qUnion([Q0])});
            skLineSegment(sketch, "E73.bottom", {"start": v(38, 17) * mm, "end": v(57, 17) * mm});
            skLineSegment(sketch, "E73.top", {"start": v(38, 23) * mm, "end": v(57, 23) * mm});
            skLineSegment(sketch, "E73.left", {"start": v(38, 17) * mm, "end": v(38, 23) * mm});
            skLineSegment(sketch, "E73.right", {"start": v(57, 17) * mm, "end": v(57, 23) * mm});
            skSolve(sketch);
        }
        {
            var Q0;
            Q0=qSketchRegion(id+"F28",true);
            extrude(context, id + "F29", {"entities" : qUnion([Q0]), "operationType" : NewBodyOperationType.ADD, "depth" : 7 * mm, "offsetDistance" : 25 * mm});
        }
        {
            var Q0;
            Q0=makeQuery(id+"F29.opExtrude","SWEPT_EDGE",EDGE,{"disambiguationData":[OSD([sQuery(id+"F28.wireOp",EDGE,"E73.bottom"),sQuery(id+"F28.wireOp",EDGE,"E73.left")])]});
            var Q1;
            Q1=makeQuery(id+"F29.opExtrude","SWEPT_EDGE",EDGE,{"disambiguationData":[OSD([sQuery(id+"F28.wireOp",EDGE,"E73.bottom"),sQuery(id+"F28.wireOp",EDGE,"E73.right")])]});
            fillet(context, id + "F30", {"entities" : qUnion([Q0, Q1]), "radius" : 2 * mm, "tangentPropagation" : true, "allowEdgeOverflow" : false});
        }
        {
            var Q0;
            Q0=makeQuery(id+"F29.opExtrude","CAP_FACE",FACE,{"disambiguationData":[OSD([sQuery(id+"F28.wireOp",EDGE,"E73.bottom"),sQuery(id+"F28.wireOp",EDGE,"E73.top"),sQuery(id+"F28.wireOp",EDGE,"E73.left"),sQuery(id+"F28.wireOp",EDGE,"E73.right")])],"isStart":false});
            var sketch = newSketch(context, id + "F31", { "sketchPlane" : qUnion([Q0])});
            skCircle(sketch, "E74", {"center": v(41, 20) * mm, "radius": 1 * mm});
            skCircle(sketch, "E75", {"center": v(54, 20) * mm, "radius": 1 * mm});
            skSolve(sketch);
        }
        {
            var Q0;
            Q0=qSketchRegion(id+"F31",true);
            var Q1;
            Q1=makeQuery(id+"F31.imprint","IMPRINT",FACE,{"disambiguationData":[TD([[makeQuery(id+"F31.imprint","IMPRINT",EDGE,{"derivedFrom":sQuery(id+"F31.wireOp",EDGE,"E74")}),1.0]])]});
            extrude(context, id + "F32", {"entities" : qUnion([Q0, Q1]), "operationType" : NewBodyOperationType.REMOVE, "oppositeDirection" : true, "depth" : 7 * mm, "offsetDistance" : 25 * mm});
        }
        {
            var Q0;
            {var subQ6=sQuery(id+"F4.wireOp",EDGE,"E18.top");Q0=makeQuery(id+"F11.imprint","IMPRINT",FACE,{"disambiguationData":[TD([[makeQuery(id+"F11.imprint","IMPRINT",EDGE,{"derivedFrom":makeQuery(id+"F5.opExtrude","CAP_EDGE",EDGE,{"disambiguationData":[OSD([subQ6])],"isStart":false})}),-1.0]])]});}
            var sketch = newSketch(context, id + "F33", { "sketchPlane" : qUnion([Q0])});
            skLineSegment(sketch, "E76.bottom", {"start": v(4, 23) * mm, "end": v(23, 23) * mm});
            skLineSegment(sketch, "E76.top", {"start": v(4, 17) * mm, "end": v(23, 17) * mm});
            skLineSegment(sketch, "E76.left", {"start": v(4, 23) * mm, "end": v(4, 17) * mm});
            skLineSegment(sketch, "E76.right", {"start": v(23, 23) * mm, "end": v(23, 17) * mm});
            skSolve(sketch);
        }
        {
            var Q0;
            Q0=qSketchRegion(id+"F33",true);
            extrude(context, id + "F34", {"entities" : qUnion([Q0]), "operationType" : NewBodyOperationType.ADD, "depth" : 5 * mm, "offsetDistance" : 25 * mm});
        }
        {
            var Q0;
            Q0=makeQuery(id+"F34.opExtrude","SWEPT_EDGE",EDGE,{"disambiguationData":[OSD([sQuery(id+"F33.wireOp",EDGE,"E76.top"),sQuery(id+"F33.wireOp",EDGE,"E76.left")])]});
            var Q1;
            Q1=makeQuery(id+"F34.opExtrude","SWEPT_EDGE",EDGE,{"disambiguationData":[OSD([sQuery(id+"F33.wireOp",EDGE,"E76.top"),sQuery(id+"F33.wireOp",EDGE,"E76.right")])]});
            fillet(context, id + "F35", {"entities" : qUnion([Q0, Q1]), "radius" : 2 * mm, "tangentPropagation" : true, "allowEdgeOverflow" : false});
        }
        {
            var Q0;
            Q0=makeQuery(id+"F34.opExtrude","CAP_FACE",FACE,{"disambiguationData":[OSD([sQuery(id+"F33.wireOp",EDGE,"E76.bottom"),sQuery(id+"F33.wireOp",EDGE,"E76.top"),sQuery(id+"F33.wireOp",EDGE,"E76.left"),sQuery(id+"F33.wireOp",EDGE,"E76.right")])],"isStart":false});
            var sketch = newSketch(context, id + "F36", { "sketchPlane" : qUnion([Q0])});
            skCircle(sketch, "E77", {"center": v(20, 20) * mm, "radius": 1 * mm});
            skCircle(sketch, "E78", {"center": v(7, 20) * mm, "radius": 1 * mm});
            skSolve(sketch);
        }
        {
            var Q0;
            Q0=qSketchRegion(id+"F36",true);
            extrude(context, id + "F37", {"entities" : qUnion([Q0]), "operationType" : NewBodyOperationType.REMOVE, "oppositeDirection" : true, "depth" : 5 * mm, "offsetDistance" : 25 * mm});
        }
        {
            var Q0;
            Q0=makeQuery(id+"F29.boolean.opBoolean","MERGE",FACE,{"derivedFrom":[makeQuery(id+"F12.boolean.opBoolean","COPY",FACE,{"derivedFrom":makeQuery(id+"F12.opExtrude","SWEPT_FACE",FACE,{"disambiguationData":[OSD([sQuery(id+"F8.wireOp",EDGE,"E47.top")])]})}),makeQuery(id+"F29.opExtrude","CAP_FACE",FACE,{"disambiguationData":[OSD([sQuery(id+"F28.wireOp",EDGE,"E73.bottom"),sQuery(id+"F28.wireOp",EDGE,"E73.top"),sQuery(id+"F28.wireOp",EDGE,"E73.left"),sQuery(id+"F28.wireOp",EDGE,"E73.right")])],"isStart":false})]});
            var sketch = newSketch(context, id + "F38", { "sketchPlane" : qUnion([Q0])});
            skLineSegment(sketch, "E79.bottom", {"start": v(43, 22) * mm, "end": v(52, 22) * mm});
            skLineSegment(sketch, "E79.top", {"start": v(43, 21) * mm, "end": v(52, 21) * mm});
            skLineSegment(sketch, "E79.left", {"start": v(43, 22) * mm, "end": v(43, 21) * mm});
            skLineSegment(sketch, "E79.right", {"start": v(52, 22) * mm, "end": v(52, 21) * mm});
            skLineSegment(sketch, "E80.bottom", {"start": v(43, 20.5) * mm, "end": v(52, 20.5) * mm});
            skLineSegment(sketch, "E80.top", {"start": v(43, 19.5) * mm, "end": v(52, 19.5) * mm});
            skLineSegment(sketch, "E80.left", {"start": v(43, 20.5) * mm, "end": v(43, 19.5) * mm});
            skLineSegment(sketch, "E80.right", {"start": v(52, 20.5) * mm, "end": v(52, 19.5) * mm});
            skLineSegment(sketch, "E81.bottom", {"start": v(43, 19) * mm, "end": v(52, 19) * mm});
            skLineSegment(sketch, "E81.top", {"start": v(43, 18) * mm, "end": v(52, 18) * mm});
            skLineSegment(sketch, "E81.left", {"start": v(43, 19) * mm, "end": v(43, 18) * mm});
            skLineSegment(sketch, "E81.right", {"start": v(52, 19) * mm, "end": v(52, 18) * mm});
            skSolve(sketch);
        }
        {
            var Q0;
            Q0=qSketchRegion(id+"F38",true);
            extrude(context, id + "F39", {"entities" : qUnion([Q0]), "operationType" : NewBodyOperationType.ADD, "depth" : 0.5 * mm, "offsetDistance" : 25 * mm});
        }
        {
            var Q0;
            Q0=makeQuery(id+"F39.opExtrude","CAP_EDGE",EDGE,{"disambiguationData":[OSD([sQuery(id+"F38.wireOp",EDGE,"E81.top")])],"isStart":false});
            var Q1;
            Q1=makeQuery(id+"F39.opExtrude","CAP_EDGE",EDGE,{"disambiguationData":[OSD([sQuery(id+"F38.wireOp",EDGE,"E81.bottom")])],"isStart":false});
            var Q2;
            Q2=makeQuery(id+"F39.opExtrude","CAP_EDGE",EDGE,{"disambiguationData":[OSD([sQuery(id+"F38.wireOp",EDGE,"E80.top")])],"isStart":false});
            var Q3;
            Q3=makeQuery(id+"F39.opExtrude","CAP_EDGE",EDGE,{"disambiguationData":[OSD([sQuery(id+"F38.wireOp",EDGE,"E80.bottom")])],"isStart":false});
            var Q4;
            Q4=makeQuery(id+"F39.opExtrude","CAP_EDGE",EDGE,{"disambiguationData":[OSD([sQuery(id+"F38.wireOp",EDGE,"E79.top")])],"isStart":false});
            var Q5;
            Q5=makeQuery(id+"F39.opExtrude","CAP_EDGE",EDGE,{"disambiguationData":[OSD([sQuery(id+"F38.wireOp",EDGE,"E79.bottom")])],"isStart":false});
            var Q6;
            Q6=makeQuery(id+"F39.opExtrude","CAP_EDGE",EDGE,{"disambiguationData":[OSD([sQuery(id+"F38.wireOp",EDGE,"E81.right")])],"isStart":false});
            var Q7;
            Q7=makeQuery(id+"F39.opExtrude","CAP_EDGE",EDGE,{"disambiguationData":[OSD([sQuery(id+"F38.wireOp",EDGE,"E80.right")])],"isStart":false});
            var Q8;
            Q8=makeQuery(id+"F39.opExtrude","CAP_EDGE",EDGE,{"disambiguationData":[OSD([sQuery(id+"F38.wireOp",EDGE,"E79.right")])],"isStart":false});
            var Q9;
            Q9=makeQuery(id+"F39.opExtrude","CAP_EDGE",EDGE,{"disambiguationData":[OSD([sQuery(id+"F38.wireOp",EDGE,"E79.left")])],"isStart":false});
            var Q10;
            Q10=makeQuery(id+"F39.opExtrude","CAP_EDGE",EDGE,{"disambiguationData":[OSD([sQuery(id+"F38.wireOp",EDGE,"E80.left")])],"isStart":false});
            var Q11;
            Q11=makeQuery(id+"F39.opExtrude","CAP_EDGE",EDGE,{"disambiguationData":[OSD([sQuery(id+"F38.wireOp",EDGE,"E81.left")])],"isStart":false});
            fillet(context, id + "F40", {"entities" : qUnion([Q0, Q1, Q2, Q3, Q4, Q5, Q6, Q7, Q8, Q9, Q10, Q11]), "radius" : 0.5 * mm, "tangentPropagation" : true, "allowEdgeOverflow" : false});
        }
        {
            var Q0;
            Q0=makeQuery(id+"F34.boolean.opBoolean","MERGE",FACE,{"derivedFrom":[makeQuery(id+"F12.boolean.opBoolean","COPY",FACE,{"derivedFrom":makeQuery(id+"F12.opExtrude","SWEPT_FACE",FACE,{"disambiguationData":[OSD([sQuery(id+"F8.wireOp",EDGE,"E50.top")])]})}),makeQuery(id+"F34.opExtrude","CAP_FACE",FACE,{"disambiguationData":[OSD([sQuery(id+"F33.wireOp",EDGE,"E76.bottom"),sQuery(id+"F33.wireOp",EDGE,"E76.top"),sQuery(id+"F33.wireOp",EDGE,"E76.left"),sQuery(id+"F33.wireOp",EDGE,"E76.right")])],"isStart":false})]});
            var sketch = newSketch(context, id + "F41", { "sketchPlane" : qUnion([Q0])});
            skLineSegment(sketch, "E82.bottom", {"start": v(8.95, 22) * mm, "end": v(17.95, 22) * mm});
            skLineSegment(sketch, "E82.top", {"start": v(8.95, 21) * mm, "end": v(17.95, 21) * mm});
            skLineSegment(sketch, "E82.left", {"start": v(8.95, 22) * mm, "end": v(8.95, 21) * mm});
            skLineSegment(sketch, "E82.right", {"start": v(17.95, 22) * mm, "end": v(17.95, 21) * mm});
            skLineSegment(sketch, "E83.bottom", {"start": v(8.95, 20.5) * mm, "end": v(17.95, 20.5) * mm});
            skLineSegment(sketch, "E83.top", {"start": v(8.95, 19.5) * mm, "end": v(17.95, 19.5) * mm});
            skLineSegment(sketch, "E83.left", {"start": v(8.95, 20.5) * mm, "end": v(8.95, 19.5) * mm});
            skLineSegment(sketch, "E83.right", {"start": v(17.95, 20.5) * mm, "end": v(17.95, 19.5) * mm});
            skLineSegment(sketch, "E84.bottom", {"start": v(8.95, 19) * mm, "end": v(17.95, 19) * mm});
            skLineSegment(sketch, "E84.top", {"start": v(8.95, 18) * mm, "end": v(17.95, 18) * mm});
            skLineSegment(sketch, "E84.left", {"start": v(8.95, 19) * mm, "end": v(8.95, 18) * mm});
            skLineSegment(sketch, "E84.right", {"start": v(17.95, 19) * mm, "end": v(17.95, 18) * mm});
            skSolve(sketch);
        }
        {
            var Q0;
            Q0=qSketchRegion(id+"F41",true);
            extrude(context, id + "F42", {"entities" : qUnion([Q0]), "operationType" : NewBodyOperationType.ADD, "depth" : 0.5 * mm, "offsetDistance" : 25 * mm});
        }
        {
            var Q0;
            Q0=makeQuery(id+"F42.opExtrude","CAP_EDGE",EDGE,{"disambiguationData":[OSD([sQuery(id+"F41.wireOp",EDGE,"E84.top")])],"isStart":false});
            var Q1;
            Q1=makeQuery(id+"F42.opExtrude","CAP_EDGE",EDGE,{"disambiguationData":[OSD([sQuery(id+"F41.wireOp",EDGE,"E84.bottom")])],"isStart":false});
            var Q2;
            Q2=makeQuery(id+"F42.opExtrude","CAP_EDGE",EDGE,{"disambiguationData":[OSD([sQuery(id+"F41.wireOp",EDGE,"E83.top")])],"isStart":false});
            var Q3;
            Q3=makeQuery(id+"F42.opExtrude","CAP_EDGE",EDGE,{"disambiguationData":[OSD([sQuery(id+"F41.wireOp",EDGE,"E83.bottom")])],"isStart":false});
            var Q4;
            Q4=makeQuery(id+"F42.opExtrude","CAP_EDGE",EDGE,{"disambiguationData":[OSD([sQuery(id+"F41.wireOp",EDGE,"E82.top")])],"isStart":false});
            var Q5;
            Q5=makeQuery(id+"F42.opExtrude","CAP_EDGE",EDGE,{"disambiguationData":[OSD([sQuery(id+"F41.wireOp",EDGE,"E82.bottom")])],"isStart":false});
            var Q6;
            Q6=makeQuery(id+"F42.opExtrude","CAP_EDGE",EDGE,{"disambiguationData":[OSD([sQuery(id+"F41.wireOp",EDGE,"E83.right")])],"isStart":false});
            var Q7;
            Q7=makeQuery(id+"F42.opExtrude","CAP_EDGE",EDGE,{"disambiguationData":[OSD([sQuery(id+"F41.wireOp",EDGE,"E84.right")])],"isStart":false});
            var Q8;
            Q8=makeQuery(id+"F42.opExtrude","CAP_EDGE",EDGE,{"disambiguationData":[OSD([sQuery(id+"F41.wireOp",EDGE,"E84.left")])],"isStart":false});
            var Q9;
            Q9=makeQuery(id+"F42.opExtrude","CAP_EDGE",EDGE,{"disambiguationData":[OSD([sQuery(id+"F41.wireOp",EDGE,"E83.left")])],"isStart":false});
            var Q10;
            Q10=makeQuery(id+"F42.opExtrude","CAP_EDGE",EDGE,{"disambiguationData":[OSD([sQuery(id+"F41.wireOp",EDGE,"E82.left")])],"isStart":false});
            var Q11;
            Q11=makeQuery(id+"F42.opExtrude","CAP_EDGE",EDGE,{"disambiguationData":[OSD([sQuery(id+"F41.wireOp",EDGE,"E82.right")])],"isStart":false});
            fillet(context, id + "F43", {"entities" : qUnion([Q0, Q1, Q2, Q3, Q4, Q5, Q6, Q7, Q8, Q9, Q10, Q11]), "radius" : 0.5 * mm, "tangentPropagation" : true, "allowEdgeOverflow" : false});
        }
        {
            var Q0;
            Q0=qCreatedBy(makeId("Top.planeOp"),FACE);
            var sketch = newSketch(context, id + "F44", { "sketchPlane" : qUnion([Q0])});
            skLineSegment(sketch, "E85.bottom", {"start": v(39.49, 55.33) * mm, "end": v(58.49, 55.33) * mm});
            skLineSegment(sketch, "E85.top", {"start": v(41.49, 49.33) * mm, "end": v(56.49, 49.33) * mm});
            skLineSegment(sketch, "E85.left", {"start": v(39.49, 55.33) * mm, "end": v(39.49, 51.33) * mm});
            skLineSegment(sketch, "E85.right", {"start": v(58.49, 55.33) * mm, "end": v(58.49, 51.33) * mm});
            skPoint(sketch, "E86.visualSharp", {"position": v(58.49, 49.33) * mm});
            skArc(sketch, "E86.filletArc", {"start": v(56.49, 49.33) * mm, "mid": v(57.9, 49.92) * mm, "end": v(58.49, 51.33) * mm});
            skPoint(sketch, "E87.visualSharp", {"position": v(39.49, 49.33) * mm});
            skArc(sketch, "E87.filletArc", {"start": v(39.49, 51.33) * mm, "mid": v(40.07, 49.92) * mm, "end": v(41.49, 49.33) * mm});
            skCircle(sketch, "E88", {"center": v(55.49, 52.33) * mm, "radius": 1 * mm});
            skCircle(sketch, "E89", {"center": v(42.49, 52.33) * mm, "radius": 1 * mm});
            skSolve(sketch);
        }
        {
            var Q0;
            Q0=qSketchRegion(id+"F44",true);
            extrude(context, id + "F45", {"entities" : qUnion([Q0]), "depth" : 2 * mm, "offsetDistance" : 25 * mm});
        }
        {
            var Q0;
            Q0=makeQuery(id+"F45.opExtrude","CAP_FACE",FACE,{"disambiguationData":[OSD([sQuery(id+"F44.wireOp",EDGE,"E85.bottom"),sQuery(id+"F44.wireOp",EDGE,"E85.top"),sQuery(id+"F44.wireOp",EDGE,"E85.left"),sQuery(id+"F44.wireOp",EDGE,"E85.right"),sQuery(id+"F44.wireOp",EDGE,"E86.filletArc"),sQuery(id+"F44.wireOp",EDGE,"E87.filletArc"),sQuery(id+"F44.wireOp",EDGE,"E88"),sQuery(id+"F44.wireOp",EDGE,"E89")])],"isStart":false});
            var sketch = newSketch(context, id + "F46", { "sketchPlane" : qUnion([Q0])});
            skCircle(sketch, "E90.0", {"center": v(55.49, 52.33) * mm, "radius": 2 * mm});
            skCircle(sketch, "E91.0", {"center": v(42.49, 52.33) * mm, "radius": 2 * mm});
            skSolve(sketch);
        }
        {
            var Q0;
            Q0=qSketchRegion(id+"F46",true);
            extrude(context, id + "F47", {"entities" : qUnion([Q0]), "operationType" : NewBodyOperationType.REMOVE, "oppositeDirection" : true, "depth" : 0.5 * mm, "offsetDistance" : 25 * mm});
        }
        {
            var Q0;
            Q0=makeQuery(id+"F45.opExtrude","SWEPT_BODY",BODY,{"disambiguationData":[OSD([sQuery(id+"F44.wireOp",EDGE,"E85.bottom"),sQuery(id+"F44.wireOp",EDGE,"E85.top"),sQuery(id+"F44.wireOp",EDGE,"E85.left"),sQuery(id+"F44.wireOp",EDGE,"E85.right"),sQuery(id+"F44.wireOp",EDGE,"E86.filletArc"),sQuery(id+"F44.wireOp",EDGE,"E87.filletArc"),sQuery(id+"F44.wireOp",EDGE,"E88"),sQuery(id+"F44.wireOp",EDGE,"E89")])]});
            transform(context, id + "F48", {"entities" : qUnion([Q0]), "transformType" : TransformType.TRANSLATION_3D, "dx" : -36.6 * mm, "dy" : -12.9 * mm, "dz" : 40 * mm, "makeCopy" : true});
        }
        {
            var Q0;
            Q0=makeQuery(id+"F48.opPattern","COPY",BODY,{"derivedFrom":makeQuery(id+"F45.opExtrude","SWEPT_BODY",BODY,{"disambiguationData":[OSD([sQuery(id+"F44.wireOp",EDGE,"E85.bottom"),sQuery(id+"F44.wireOp",EDGE,"E85.top"),sQuery(id+"F44.wireOp",EDGE,"E85.left"),sQuery(id+"F44.wireOp",EDGE,"E85.right"),sQuery(id+"F44.wireOp",EDGE,"E86.filletArc"),sQuery(id+"F44.wireOp",EDGE,"E87.filletArc"),sQuery(id+"F44.wireOp",EDGE,"E88"),sQuery(id+"F44.wireOp",EDGE,"E89")])]}),"instanceName":"1"});
            deleteBodies(context, id + "F49", {"entities" : qUnion([Q0])});
        }
        {
            var Q0;
            Q0=makeQuery(id+"F45.opExtrude","SWEPT_BODY",BODY,{"disambiguationData":[OSD([sQuery(id+"F44.wireOp",EDGE,"E85.bottom"),sQuery(id+"F44.wireOp",EDGE,"E85.top"),sQuery(id+"F44.wireOp",EDGE,"E85.left"),sQuery(id+"F44.wireOp",EDGE,"E85.right"),sQuery(id+"F44.wireOp",EDGE,"E86.filletArc"),sQuery(id+"F44.wireOp",EDGE,"E87.filletArc"),sQuery(id+"F44.wireOp",EDGE,"E88"),sQuery(id+"F44.wireOp",EDGE,"E89")])]});
            transform(context, id + "F50", {"entities" : qUnion([Q0]), "transformType" : TransformType.TRANSLATION_3D, "dx" : -31.9 * mm, "dy" : 0 * mm, "dz" : 0 * mm, "makeCopy" : true});
        }
    });
